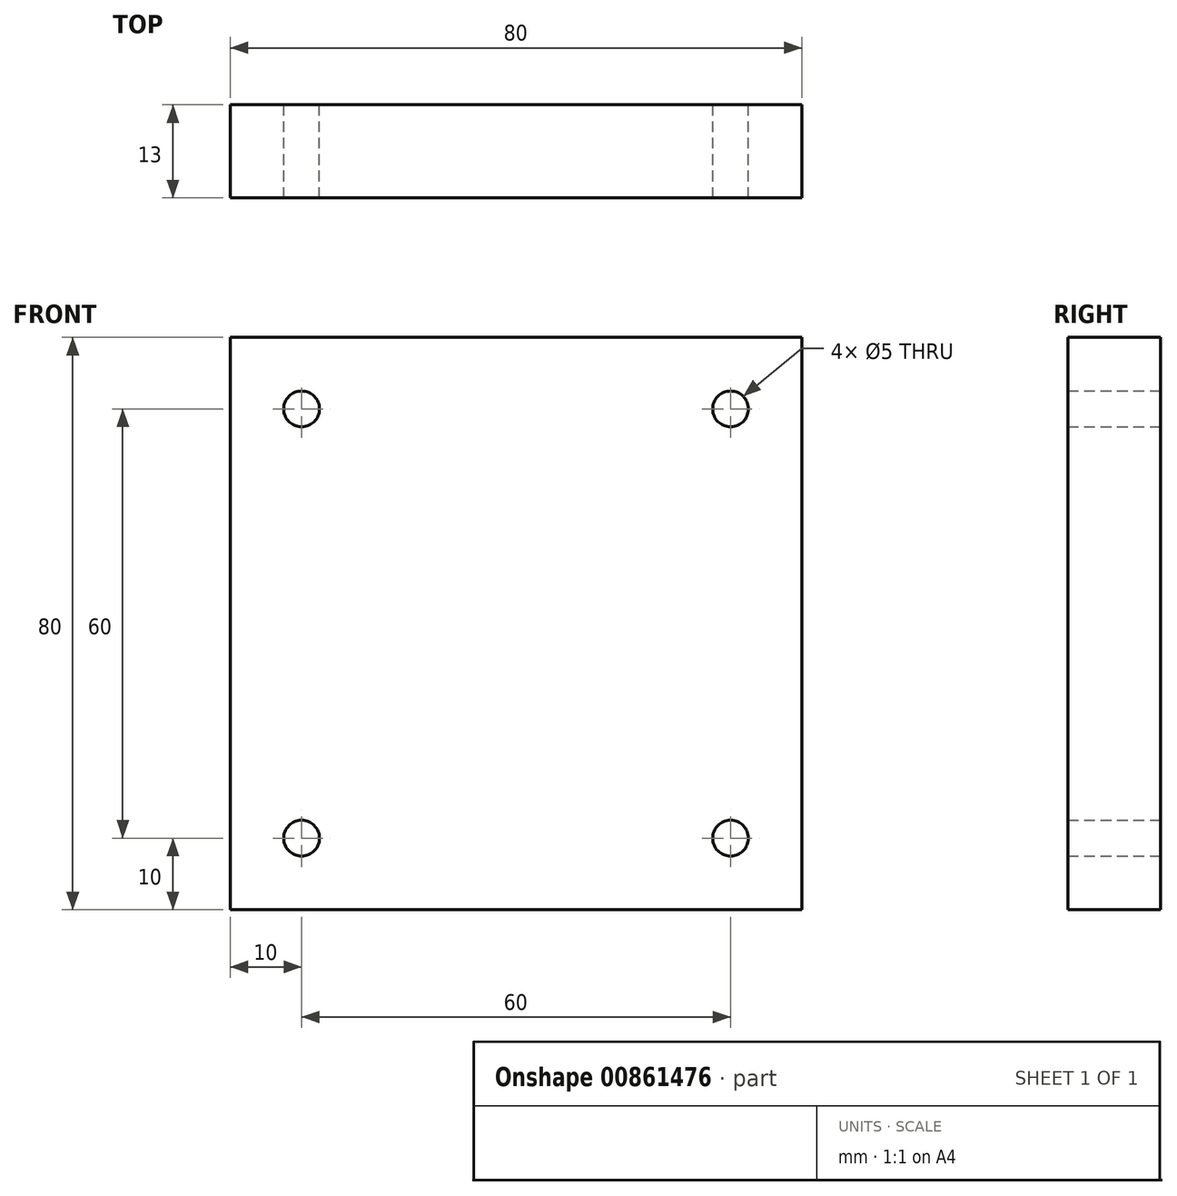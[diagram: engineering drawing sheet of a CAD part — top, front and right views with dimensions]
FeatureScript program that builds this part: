
annotation { "Feature Type Name" : "Feature", "Feature Type Description" : "" }
export const myFeature = defineFeature(function(context is Context, id is Id, definition is map)
    precondition{}
    {
        {
            var Q0;
            Q0=qCreatedBy(makeId("Front.planeOp"),FACE);
            var sketch = newSketch(context, id + "F0", { "sketchPlane" : qUnion([Q0])});
            skLineSegment(sketch, "E0.bottom", {"start": v(0, 0) * mm, "end": v(80, 0) * mm});
            skLineSegment(sketch, "E0.top", {"start": v(0, 80) * mm, "end": v(80, 80) * mm});
            skLineSegment(sketch, "E0.left", {"start": v(0, 0) * mm, "end": v(0, 80) * mm});
            skLineSegment(sketch, "E0.right", {"start": v(80, 0) * mm, "end": v(80, 80) * mm});
            skLineSegment(sketch, "E1.0", {"start": v(10, 70) * mm, "end": v(70, 70) * mm, "construction": true});
            skLineSegment(sketch, "E1.1", {"start": v(10, 10) * mm, "end": v(10, 70) * mm, "construction": true});
            skLineSegment(sketch, "E1.2", {"start": v(10, 10) * mm, "end": v(70, 10) * mm, "construction": true});
            skLineSegment(sketch, "E1.3", {"start": v(70, 10) * mm, "end": v(70, 70) * mm, "construction": true});
            skPoint(sketch, "E2", {"position": v(70, 70) * mm});
            skPoint(sketch, "E3", {"position": v(70, 10) * mm});
            skPoint(sketch, "E4", {"position": v(10, 10) * mm});
            skPoint(sketch, "E5", {"position": v(10, 70) * mm});
            skSolve(sketch);
        }
        {
            var Q0;
            Q0 = qSketchRegion(id + "F0", true);
            extrude(context, id + "F1", {"entities" : qUnion([Q0]), "depth" : 13 * mm, "offsetDistance" : 25 * mm});
        }
        {
            var Q0;
            Q0=sQuery(id+"F0.wireOp",VERTEX,"E5");
            var Q1;
            Q1=sQuery(id+"F0.wireOp",VERTEX,"E2");
            var Q2;
            Q2=sQuery(id+"F0.wireOp",VERTEX,"E3");
            var Q3;
            Q3=sQuery(id+"F0.wireOp",VERTEX,"E4");
            var Q4;
            Q4=makeQuery(id+"F1.opExtrude","SWEPT_BODY",BODY,{"disambiguationData":[OSD([sQuery(id+"F0.wireOp",EDGE,"E0.bottom"),sQuery(id+"F0.wireOp",EDGE,"E0.top"),sQuery(id+"F0.wireOp",EDGE,"E0.left"),sQuery(id+"F0.wireOp",EDGE,"E0.right")])]});
            hole(context, id + "F2", {"style" : HoleStyle.SIMPLE, "endStyle" : HoleEndStyle.THROUGH, "oppositeDirection" : true, "holeDiameter" : 5 * mm, "majorDiameter" : 5 * mm, "isTappedThrough" : true, "tappedDepth" : 12 * mm, "tapClearance" : 3, "startFromSketch" : true, "locations" : qUnion([Q0, Q1, Q2, Q3]), "scope" : qUnion([Q4])});
        }
    });
